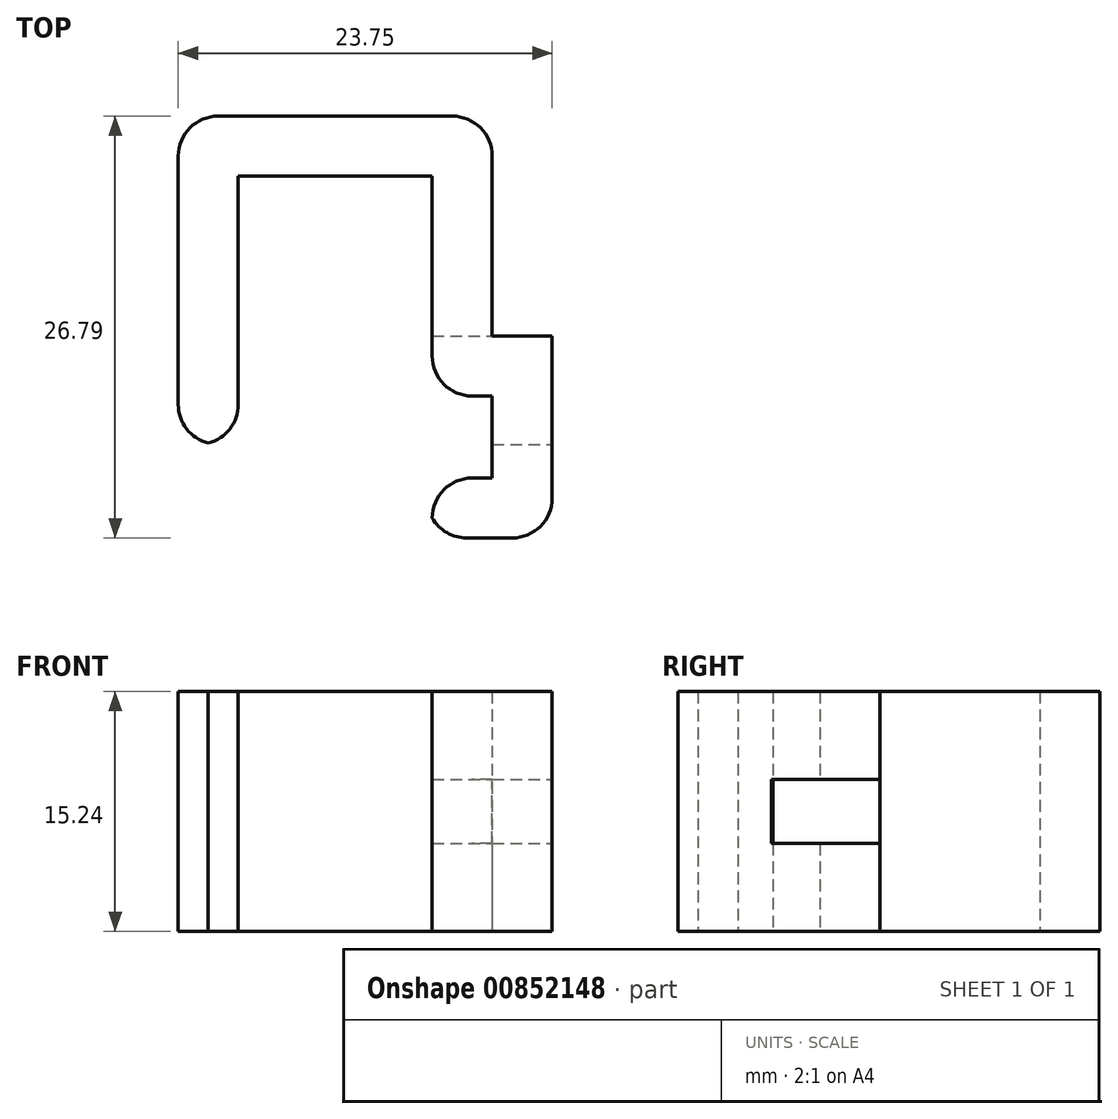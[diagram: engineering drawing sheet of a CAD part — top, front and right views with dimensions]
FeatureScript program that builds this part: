
annotation { "Feature Type Name" : "Feature", "Feature Type Description" : "" }
export const myFeature = defineFeature(function(context is Context, id is Id, definition is map)
    precondition{}
    {
        {
            var Q0;
            Q0=qCreatedBy(makeId("Top.planeOp"),FACE);
            var sketch = newSketch(context, id + "F0", { "sketchPlane" : qUnion([Q0])});
            skLineSegment(sketch, "E0", {"start": v(0, 0) * mm, "end": v(3.8, 0) * mm});
            skLineSegment(sketch, "E1", {"start": v(3.8, 0) * mm, "end": v(3.8, 17.04) * mm});
            skLineSegment(sketch, "E2", {"start": v(3.8, 17.04) * mm, "end": v(16.13, 17.04) * mm});
            skLineSegment(sketch, "E3", {"start": v(16.13, 17.04) * mm, "end": v(16.13, 0) * mm});
            skLineSegment(sketch, "E4", {"start": v(19.94, 3.07) * mm, "end": v(19.94, -2.13) * mm});
            skLineSegment(sketch, "E5", {"start": v(19.94, -2.13) * mm, "end": v(16.13, -2.13) * mm});
            skLineSegment(sketch, "E6", {"start": v(16.13, -2.13) * mm, "end": v(16.13, -5.94) * mm});
            skLineSegment(sketch, "E7", {"start": v(16.13, -5.94) * mm, "end": v(23.75, -5.94) * mm});
            skLineSegment(sketch, "E8", {"start": v(23.75, -5.94) * mm, "end": v(23.75, 6.88) * mm});
            skLineSegment(sketch, "E9", {"start": v(23.75, 6.88) * mm, "end": v(19.94, 6.88) * mm});
            skLineSegment(sketch, "E10", {"start": v(19.94, 6.88) * mm, "end": v(19.94, 20.85) * mm});
            skLineSegment(sketch, "E11", {"start": v(19.94, 20.85) * mm, "end": v(0, 20.85) * mm});
            skLineSegment(sketch, "E12", {"start": v(0, 20.85) * mm, "end": v(0, 0) * mm});
            skLineSegment(sketch, "E13", {"start": v(19.94, 3.07) * mm, "end": v(16.13, 3.07) * mm});
            skLineSegment(sketch, "E14", {"start": v(16.13, 3.07) * mm, "end": v(16.13, 0) * mm});
            skPoint(sketch, "E15.orphan", {"position": v(19.94, 0) * mm});
            skSolve(sketch);
        }
        {
            var Q0;
            Q0=makeQuery(id+"F0.imprint","IMPRINT",FACE,{"disambiguationData":[TD([[makeQuery(id+"F0.imprint","IMPRINT",EDGE,{"derivedFrom":sQuery(id+"F0.wireOp",EDGE,"E0")}),1.0]])]});
            extrude(context, id + "F1", {"entities" : qUnion([Q0]), "depth" : 15.24 * mm, "offsetDistance" : 25.4 * mm});
        }
        {
            var Q0;
            Q0=makeQuery(id+"F1.opExtrude","SWEPT_FACE",FACE,{"disambiguationData":[OSD([sQuery(id+"F0.wireOp",EDGE,"E8")])]});
            var sketch = newSketch(context, id + "F2", { "sketchPlane" : qUnion([Q0])});
            skLineSegment(sketch, "E16.top", {"start": v(6.88, 5.59) * mm, "end": v(0, 5.59) * mm});
            skLineSegment(sketch, "E16.left", {"start": v(6.88, 7.62) * mm, "end": v(6.88, 5.59) * mm});
            skLineSegment(sketch, "E16.right", {"start": v(0, 7.62) * mm, "end": v(0, 5.59) * mm});
            skLineSegment(sketch, "E17.top", {"start": v(6.88, 9.65) * mm, "end": v(0, 9.65) * mm});
            skLineSegment(sketch, "E17.left", {"start": v(6.88, 7.62) * mm, "end": v(6.88, 9.65) * mm});
            skLineSegment(sketch, "E17.right", {"start": v(0, 7.62) * mm, "end": v(0, 9.65) * mm});
            skSolve(sketch);
        }
        {
            var Q0;
            Q0=makeQuery(id+"F2.imprint","IMPRINT",FACE,{"disambiguationData":[TD([[makeQuery(id+"F2.imprint","IMPRINT",EDGE,{"derivedFrom":sQuery(id+"F2.wireOp",EDGE,"E16.top")}),-1.0]])]});
            extrude(context, id + "F3", {"entities" : qUnion([Q0]), "operationType" : NewBodyOperationType.REMOVE, "oppositeDirection" : true, "depth" : 9.78 * mm, "offsetDistance" : 25.4 * mm});
        }
        {
            var Q0;
            Q0=makeQuery(id+"F1.opExtrude","SWEPT_EDGE",EDGE,{"disambiguationData":[OSD([sQuery(id+"F0.wireOp",EDGE,"E11"),sQuery(id+"F0.wireOp",EDGE,"E12")])]});
            var Q1;
            Q1=makeQuery(id+"F1.opExtrude","SWEPT_EDGE",EDGE,{"disambiguationData":[OSD([sQuery(id+"F0.wireOp",EDGE,"E10"),sQuery(id+"F0.wireOp",EDGE,"E11")])]});
            var Q2;
            Q2=makeQuery(id+"F1.opExtrude","SWEPT_EDGE",EDGE,{"disambiguationData":[OSD([sQuery(id+"F0.wireOp",EDGE,"E7"),sQuery(id+"F0.wireOp",EDGE,"E8")])]});
            var Q3;
            Q3=makeQuery(id+"F1.opExtrude","SWEPT_EDGE",EDGE,{"disambiguationData":[OSD([sQuery(id+"F0.wireOp",EDGE,"E5"),sQuery(id+"F0.wireOp",EDGE,"E6")])]});
            fillet(context, id + "F4", {"entities" : qUnion([Q0, Q1, Q2, Q3]), "radius" : 2.54 * mm, "tangentPropagation" : true, "allowEdgeOverflow" : false});
        }
        {
            var Q0;
            Q0=makeQuery(id+"F1.opExtrude","SWEPT_EDGE",EDGE,{"disambiguationData":[OSD([sQuery(id+"F0.wireOp",EDGE,"E0"),sQuery(id+"F0.wireOp",EDGE,"E12")])]});
            var Q1;
            Q1=makeQuery(id+"F1.opExtrude","SWEPT_EDGE",EDGE,{"disambiguationData":[OSD([sQuery(id+"F0.wireOp",EDGE,"E0"),sQuery(id+"F0.wireOp",EDGE,"E1")])]});
            var Q2;
            Q2=makeQuery(id+"F1.opExtrude","SWEPT_EDGE",EDGE,{"disambiguationData":[OSD([sQuery(id+"F0.wireOp",EDGE,"E6"),sQuery(id+"F0.wireOp",EDGE,"E7")])]});
            var Q3;
            {var subQ0=sQuery(id+"F0.wireOp",EDGE,"E13");var subQ1=sQuery(id+"F0.wireOp",EDGE,"E3");Q3=makeQuery(id+"F3.boolean.opBoolean","SPLIT",EDGE,{"disambiguationData":[TD([makeQuery(id+"F3.opExtrude","SWEPT_FACE",FACE,{"disambiguationData":[OSD([sQuery(id+"F2.wireOp",EDGE,"E16.top")])]})])],"derivedFrom":makeQuery(id+"F1.opExtrude","SWEPT_EDGE",EDGE,{"disambiguationData":[OSD([subQ1,subQ0])]})});}
            var Q4;
            {var subQ0=sQuery(id+"F0.wireOp",EDGE,"E13");var subQ1=sQuery(id+"F0.wireOp",EDGE,"E3");Q4=makeQuery(id+"F3.boolean.opBoolean","SPLIT",EDGE,{"disambiguationData":[TD([makeQuery(id+"F3.opExtrude","SWEPT_FACE",FACE,{"disambiguationData":[OSD([sQuery(id+"F2.wireOp",EDGE,"E17.top")])]})])],"derivedFrom":makeQuery(id+"F1.opExtrude","SWEPT_EDGE",EDGE,{"disambiguationData":[OSD([subQ1,subQ0])]})});}
            fillet(context, id + "F5", {"entities" : qUnion([Q0, Q1, Q2, Q3, Q4]), "radius" : 2.54 * mm, "tangentPropagation" : true, "allowEdgeOverflow" : false});
        }
    });
